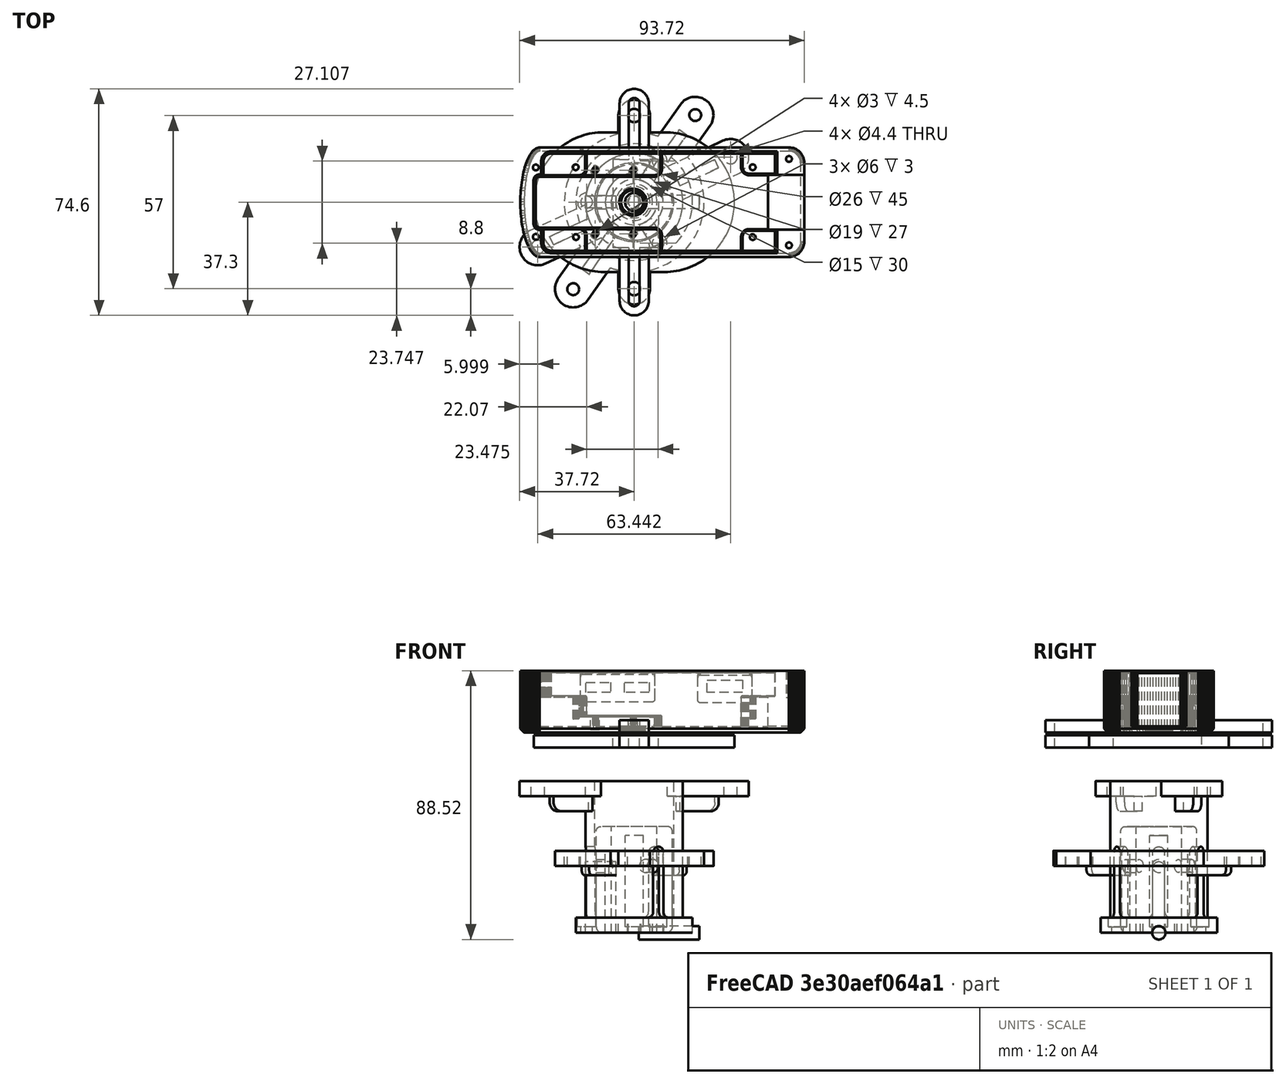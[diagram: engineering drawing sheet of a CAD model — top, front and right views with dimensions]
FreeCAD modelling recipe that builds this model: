
FCSTD DOCUMENT  (FreeCAD 0.19R)
Label: microscope_camera_adapter_less_bolts
License: All rights reserved
LicenseURL: http://en.wikipedia.org/wiki/All_rights_reserved
objects: Part::Cylinder×18, Part::MultiFuse×12, Part::FeaturePython×9, Part::Cut×7, Part::Box×6, Part::Fillet×5, App::Part×3, Part::Feature×2, Spreadsheet::Sheet×1
note: 50 computed .brp shape members not serialized (recipe doc carries the construction recipe); baked Part::Feature solids carry a one-line shape summary decoded from their .brp

FEATURE [Spreadsheet::Sheet] Spreadsheet  label="p"
  cells = A1=plug_h; B1(plug_h)==30mm; A2=plug_central_hole_r; B2(plug_central_hole_r)==15mm; A3=plug_wall; B3(plug_wall)==5mm; A4=plug_wall_gap; B4(plug_wall_gap)==0.5mm; A5=top_block_h; B5(top_block_h)==47mm; A6=top_block_wall; B6(top_block_wall)==3mm; A7=top_block_bottom_wall; B7(top_block_bottom_wall)==2mm; A8=bolt_hole_r; B8(bolt_hole_r)==1.95mm; A9=insert_hole_r; B9(insert_hole_r)==2.2mm; A10=bolt_hole_size; B10(bolt_hole_size)==15mm; A11=plug_hole_z; B11(plug_hole_z)==5mm; A12=top_block_hole_offset_z; B12(top_block_hole_offset_z)==10mm; A13=camera_attachment_wall; B13(camera_attachment_wall)==5mm; A14=camera_attachment_h; B14(camera_attachment_h)==4mm; A15=top_attachment_disk_r; B15(top_attachment_disk_r)==19.2mm; A16=top_attachment_disk_h; B16(top_attachment_disk_h)==5mm; A17=top_attachment_hole_r; B17(top_attachment_hole_r)==11.5mm; A18=bolt_head_h; B18(bolt_head_h)==3mm; A19=bolt_head_r; B19(bolt_head_r)==3mm; A20=top_attachment_expanding_h; B20(top_attachment_expanding_h)==10mm; A21=top_attachment_expanding_r; B21(top_attachment_expanding_r)==top_attachment_disk_r + top_block_wall + 1mm; A22=top_lower_part_h; B22(top_lower_part_h)==30mm; A23=inserter_wall; B23(inserter_wall)==5mm; A24=inserter_hole_pos; B24(inserter_hole_pos)==13mm; A25=middle_part_h; B25(middle_part_h)==45mm; A26=middle_bolt_hole_size; B26(middle_bolt_hole_size)==top_lower_part_h - inserter_hole_pos + insert_hole_r * 2; A27=spring_r; B27(spring_r)==5mm; A28=spring_border; B28(spring_border)==1mm; A29=sprint_dist; B29(sprint_dist)==70mm; A30=outer_cylinder_r; B30(outer_cylinder_r)==top_attachment_hole_r + 1mm; A31=zero_holder_h; B31(zero_holder_h)==27mm
FEATURE [Part::Feature] Compound001  label="RPI compound001"
  Placement = pos=(0,0,61) rot=(0,0,1;3.14159rad)
  shape: bbox 109.5 x 74.6 x 20.32 mm, 7782 faces (baked)
FEATURE [Part::Cylinder] Cylinder016  label="outer cylinder"
  Angle = 360
  AttacherType = Attacher::AttachEngine3D
  Height = 35
  Radius = 12.5
  expr: Radius = <<p>>.outer_cylinder_r
  expr: Height = <<p>>.top_lower_part_h + <<p>>.top_attachment_disk_h
FEATURE [Part::Cylinder] Cylinder018  label="top attachment bolt hole001"
  Angle = 360
  AttacherType = Attacher::AttachEngine3D
  Height = 30
  Radius = 1.95
  expr: Radius = <<p>>.bolt_hole_r
FEATURE [Part::Cylinder] Cylinder019  label="top attachment disk001"
  Angle = 360
  AttacherType = Attacher::AttachEngine3D
  Height = 5
  Radius = 19.2
  expr: Radius = <<p>>.top_attachment_disk_r
  expr: Height = <<p>>.top_attachment_disk_h
FEATURE [Part::Cylinder] Cylinder020  label="inner cylinder"
  Angle = 360
  AttacherType = Attacher::AttachEngine3D
  Height = 52
  Radius = 7.5
  expr: Height = <<p>>.top_block_h + <<p>>.top_attachment_disk_h
  expr: Radius = <<p>>.outer_cylinder_r - <<p>>.inserter_wall
FEATURE [Part::Cylinder] Cylinder021  label="top attachment bolt head hole001"
  Angle = 360
  AttacherType = Attacher::AttachEngine3D
  Height = 30
  Placement = pos=(0,0,2) rot=(0,0,1;0rad)
  Radius = 3
  expr: Radius = <<p>>.bolt_head_r
  expr: .Placement.Base.z = <<p>>.top_attachment_disk_h - <<p>>.bolt_head_h
FEATURE [Part::MultiFuse] Fusion011  label="bolt hole fusion002"
  Shapes = -> [Cylinder018,Cylinder021]
FEATURE [Part::FeaturePython] Array007  label="top attachment bolt hole array001"  # Draft array (typed FeaturePython)
  Angle = 360
  ArrayType = 2
  Axis = (0,0,1)
  Base = -> Fusion011
  Center = (0,0,0)
  Count = 4
  ExpandArray = false
  Fuse = false
  IntervalAxis = (0,0,0)
  IntervalX = (50,0,0)
  IntervalY = (0,50,0)
  IntervalZ = (0,0,50)
  NumberCircles = 2
  NumberPolar = 5
  NumberX = 2
  NumberY = 2
  NumberZ = 1
  PlacementList = 4 placements: [(0,0,0),(-15.65,0,0),(7.825,-13.5533,0),(7.825,13.5533,0)]
  RadialDistance = 15.65
  ScaleList = (4) [(1,1,1),(1,1,1),(1,1,1),(1,1,1)]
  Symmetry = 1
  TangentialDistance = 30
  expr: RadialDistance = <<p>>.top_attachment_hole_r + (<<p>>.top_attachment_disk_r - <<p>>.top_attachment_hole_r) / 2 + 0.3mm
FEATURE [Part::Cylinder] Cylinder023  label="insert hole001"
  Angle = 360
  AttacherType = Attacher::AttachEngine3D
  Height = 20
  Placement = pos=(21.5,0,0) rot=(0,-1,0;1.5708rad)
  Radius = 2.2
  expr: .Placement.Base.x = <<p>>.top_attachment_hole_r + Height / 2
  expr: Radius = <<p>>.insert_hole_r
FEATURE [Part::FeaturePython] Array009  label="insert hole polar array001"  # Draft array (typed FeaturePython)
  Angle = 360
  ArrayType = 1
  Axis = (0,0,1)
  Base = -> Cylinder023
  Center = (0,0,0)
  Count = 3
  ExpandArray = false
  Fuse = false
  IntervalAxis = (0,0,0)
  IntervalX = (50,0,0)
  IntervalY = (0,50,0)
  IntervalZ = (0,0,50)
  NumberCircles = 3
  NumberPolar = 3
  NumberX = 2
  NumberY = 2
  NumberZ = 1
  Placement = pos=(0,0,22) rot=(0,0,1;1.0472rad)
  PlacementList = 3 placements: [(21.5,0,0),(-10.75,18.6195,0),(-10.75,-18.6195,0)]
  RadialDistance = 50
  ScaleList = (3) [(1,1,1),(1,1,1),(1,1,1)]
  Symmetry = 1
  TangentialDistance = 25
  expr: .Placement.Base.z = <<p>>.top_attachment_disk_h + <<p>>.top_lower_part_h - <<p>>.inserter_hole_pos
FEATURE [Part::MultiFuse] Fusion010  label="top attachment hole fusion001"
  Shapes = -> [Array009,Cylinder020]
FEATURE [Part::Cut] Cut007  label="top lower pipe"
  Base = -> Cylinder016
  Tool = -> Cylinder020
FEATURE [Part::Fillet] Fillet002  label="top lower pipe fillet"
  Base = -> Cut007
  Edges = 1 edges r=1.5: [Edge1]
FEATURE [Part::MultiFuse] Fusion012  label="body fusion001"
  Shapes = -> [Cylinder019,Fillet002]
FEATURE [Part::Cylinder] Cylinder024  label="internal cylinder"
  Angle = 360
  AttacherType = Attacher::AttachEngine3D
  Height = 45
  Placement = pos=(0,0,5) rot=(0,0,1;0rad)
  Radius = 13
  expr: .Placement.Base.z = <<p>>.top_attachment_disk_h
  expr: Height = <<p>>.middle_part_h
  expr: Radius = <<p>>.outer_cylinder_r + <<p>>.plug_wall_gap
FEATURE [Part::Cylinder] Cylinder025  label="external cylinder001"
  Angle = 360
  AttacherType = Attacher::AttachEngine3D
  Height = 45
  Placement = pos=(0,0,5) rot=(0,0,1;0rad)
  Radius = 16
  expr: .Placement.Base.z = <<p>>.top_attachment_disk_h
  expr: Height = <<p>>.middle_part_h
  expr: Radius = <<internal cylinder>>.Radius + <<p>>.top_block_wall
FEATURE [Part::Cylinder] Cylinder026  label="hole side001"
  Angle = 360
  AttacherType = Attacher::AttachEngine3D
  Height = 10
  Placement = pos=(21.4,0,0) rot=(0,0,1;0rad)
  Radius = 1.95
  expr: .Placement.Base.x = <<p>>.middle_bolt_hole_size
  expr: Radius = <<p>>.bolt_hole_r
FEATURE [Part::Box] Box002  label="camera hole central cube001"
  AttacherType = Attacher::AttachEngine3D
  Height = 10
  Length = 21.4
  Placement = pos=(0,-1.95,0) rot=(0,0,1;0rad)
  Width = 3.9
  expr: .Placement.Base.y = -<<p>>.bolt_hole_r
  expr: Width = <<p>>.bolt_hole_r * 2
  expr: Length = <<p>>.middle_bolt_hole_size
FEATURE [Part::MultiFuse] Fusion013  label="bolt hole fusion003"
  Placement = pos=(-6,0,0) rot=(0,-1,0;1.5708rad)
  Shapes = -> [Box002,Cylinder026]
  expr: .Placement.Base.x = -<<external cylinder001>>.Radius + <<hole side001>>.Height
FEATURE [Part::FeaturePython] Array011  label="bolt hole polar array001"  # Draft array (typed FeaturePython)
  Angle = 360
  ArrayType = 1
  Axis = (0,0,1)
  Base = -> Fusion013
  Center = (0,0,0)
  Count = 3
  ExpandArray = false
  Fuse = false
  IntervalAxis = (0,0,0)
  IntervalX = (50,0,0)
  IntervalY = (0,50,0)
  IntervalZ = (0,0,50)
  NumberCircles = 3
  NumberPolar = 3
  NumberX = 2
  NumberY = 2
  NumberZ = 1
  Placement = pos=(0,0,5) rot=(0,0,1;0rad)
  PlacementList = 3 placements: [(-6,0,0),(3,-5.19615,0),(3,5.19615,0)]
  RadialDistance = 50
  ScaleList = (3) [(1,1,1),(1,1,1),(1,1,1)]
  Symmetry = 1
  TangentialDistance = 25
  expr: .Placement.Base.z = <<external cylinder001>>.Placement.Base.z
FEATURE [Part::MultiFuse] Fusion014  label="middle hole fusion"
  Shapes = -> [Array011,Cylinder024]
FEATURE [Part::Cylinder] Cylinder027  label="spring plate end"
  Angle = 360
  AttacherType = Attacher::AttachEngine3D
  Height = 5
  Radius = 6
  expr: Height = <<p>>.inserter_wall
  expr: Radius = <<p>>.spring_r + <<p>>.spring_border
FEATURE [Part::FeaturePython] Array012  label="spring plate end array"  # Draft array (typed FeaturePython)
  Angle = 360
  ArrayType = 0
  Axis = (0,0,1)
  Base = -> Cylinder027
  Center = (0,0,0)
  Count = 2
  ExpandArray = false
  Fuse = false
  IntervalAxis = (0,0,0)
  IntervalX = (70,0,0)
  IntervalY = (0,100,0)
  IntervalZ = (0,0,100)
  NumberCircles = 3
  NumberPolar = 5
  NumberX = 2
  NumberY = 1
  NumberZ = 1
  PlacementList = 2 placements: [(0,0,0),(70,0,0)]
  RadialDistance = 50
  ScaleList = (2) [(1,1,1),(1,1,1)]
  Symmetry = 1
  TangentialDistance = 25
  expr: .IntervalX.x = <<p>>.sprint_dist
FEATURE [Part::Cylinder] Cylinder028  label="spring plate end001"
  Angle = 360
  AttacherType = Attacher::AttachEngine3D
  Height = 5
  Radius = 2.2
  expr: Radius = <<p>>.insert_hole_r
  expr: Height = <<p>>.inserter_wall
FEATURE [Part::FeaturePython] Array013  label="spring plate end array001"  # Draft array (typed FeaturePython)
  Angle = 360
  ArrayType = 0
  Axis = (0,0,1)
  Base = -> Cylinder028
  Center = (0,0,0)
  Count = 2
  ExpandArray = false
  Fuse = false
  IntervalAxis = (0,0,0)
  IntervalX = (70,0,0)
  IntervalY = (0,100,0)
  IntervalZ = (0,0,100)
  NumberCircles = 3
  NumberPolar = 5
  NumberX = 2
  NumberY = 1
  NumberZ = 1
  PlacementList = 2 placements: [(0,0,0),(70,0,0)]
  RadialDistance = 50
  ScaleList = (2) [(1,1,1),(1,1,1)]
  Symmetry = 1
  TangentialDistance = 25
  expr: .IntervalX.x = <<p>>.sprint_dist
FEATURE [Part::Box] Box003  label="spring plate cube"
  AttacherType = Attacher::AttachEngine3D
  Height = 5
  Length = 70
  Placement = pos=(0,-6,0) rot=(0,0,1;0rad)
  Width = 12
  expr: .Placement.Base.y = -Width / 2
  expr: Height = <<spring plate end>>.Height
  expr: Width = <<spring plate end>>.Radius * 2
  expr: Length = <<p>>.sprint_dist
FEATURE [Part::Cylinder] Cylinder029  label="spring plate end002"
  Angle = 360
  AttacherType = Attacher::AttachEngine3D
  Height = 5
  Radius = 6
  expr: Radius = <<p>>.spring_r + <<p>>.spring_border
  expr: Height = <<p>>.inserter_wall
FEATURE [Part::FeaturePython] Array014  label="spring plate end array002"  # Draft array (typed FeaturePython)
  Angle = 360
  ArrayType = 0
  Axis = (0,0,1)
  Base = -> Cylinder029
  Center = (0,0,0)
  Count = 2
  ExpandArray = false
  Fuse = false
  IntervalAxis = (0,0,0)
  IntervalX = (70,0,0)
  IntervalY = (0,100,0)
  IntervalZ = (0,0,100)
  NumberCircles = 3
  NumberPolar = 5
  NumberX = 2
  NumberY = 1
  NumberZ = 1
  PlacementList = 2 placements: [(0,0,0),(70,0,0)]
  RadialDistance = 50
  ScaleList = (2) [(1,1,1),(1,1,1)]
  Symmetry = 1
  TangentialDistance = 25
  expr: .IntervalX.x = <<p>>.sprint_dist
FEATURE [Part::Cylinder] Cylinder030  label="spring plate end003"
  Angle = 360
  AttacherType = Attacher::AttachEngine3D
  Height = 5
  Radius = 1.95
  expr: Height = <<p>>.inserter_wall
  expr: Radius = <<p>>.bolt_hole_r
FEATURE [Part::FeaturePython] Array015  label="spring plate end array003"  # Draft array (typed FeaturePython)
  Angle = 360
  ArrayType = 0
  Axis = (0,0,1)
  Base = -> Cylinder030
  Center = (0,0,0)
  Count = 2
  ExpandArray = false
  Fuse = false
  IntervalAxis = (0,0,0)
  IntervalX = (70,0,0)
  IntervalY = (0,100,0)
  IntervalZ = (0,0,100)
  NumberCircles = 3
  NumberPolar = 5
  NumberX = 2
  NumberY = 1
  NumberZ = 1
  PlacementList = 2 placements: [(0,0,0),(70,0,0)]
  RadialDistance = 50
  ScaleList = (2) [(1,1,1),(1,1,1)]
  Symmetry = 1
  TangentialDistance = 25
  expr: .IntervalX.x = <<p>>.sprint_dist
FEATURE [Part::Box] Box004  label="Cube"
  AttacherType = Attacher::AttachEngine3D
  Height = 5
  Length = 70
  Placement = pos=(0,-6,0) rot=(0,0,1;0rad)
  Width = 12
  expr: Length = <<p>>.sprint_dist
  expr: Width = <<spring plate end002>>.Radius * 2
  expr: Height = <<p>>.inserter_wall
  expr: .Placement.Base.y = -Width / 2
FEATURE [Part::MultiFuse] Fusion017  label="spring plate fusion001"
  Shapes = -> [Array014,Box004]
FEATURE [Part::Cut] Cut010  label="spring attachment plate001"
  Base = -> Fusion017
  Placement = pos=(-35,0,22) rot=(0,0,1;0rad)
  Tool = -> Array015
  expr: .Placement.Base.z = <<zero holder external cylinder>>.Height - <<spring plate end002>>.Height
  expr: .Placement.Base.x = -<<p>>.sprint_dist / 2
FEATURE [Part::Cylinder] Cylinder031  label="zero holder external cylinder"
  Angle = 360
  AttacherType = Attacher::AttachEngine3D
  Height = 27
  Radius = 12.5
  expr: Height = <<p>>.zero_holder_h
  expr: Radius = <<internal cylinder>>.Radius - <<p>>.plug_wall_gap
FEATURE [Part::Cylinder] Cylinder032  label="zero holder internal cylinder"
  Angle = 360
  AttacherType = Attacher::AttachEngine3D
  Height = 27
  Radius = 9.5
  expr: Radius = <<zero holder external cylinder>>.Radius - <<p>>.top_block_wall
  expr: Height = <<p>>.zero_holder_h
FEATURE [Part::Cylinder] Cylinder035  label="zero holder top disk"
  Angle = 360
  AttacherType = Attacher::AttachEngine3D
  Height = 5
  Placement = pos=(0,0,22) rot=(0,0,1;0rad)
  Radius = 23
  expr: .Placement.Base.z = <<zero holder external cylinder>>.Height - Height
  expr: Height = <<spring plate end002>>.Height
FEATURE [Part::Feature] Cut002004001  label="Pi_Zero_Case001"
  Placement = pos=(0,0,66) rot=(0,0,1;3.14159rad)
  shape: bbox 93.47 x 74.6 x 20.32 mm, 7631 faces, 7 solids (baked)
FEATURE [Part::Box] Box007  label="spring plate cube001"
  AttacherType = Attacher::AttachEngine3D
  Height = 5
  Length = 60
  Placement = pos=(5,-1.5,-5) rot=(0,0,1;0rad)
  Width = 3
  expr: .Placement.Base.z = -<<spring plate end>>.Height
  expr: Length = <<p>>.sprint_dist - 10mm
  expr: Height = <<spring plate end>>.Height
  expr: .Placement.Base.y = -Width / 2
FEATURE [Part::Fillet] Fillet003
  Base = -> Box007
  Edges = 2 edges r=3: [Edge4,Edge8]
FEATURE [Part::MultiFuse] Fusion015  label="spring plate fusion"
  Shapes = -> [Array012,Box003,Fillet003]
FEATURE [Part::Cut] Cut009  label="spring attachment plate"
  Base = -> Fusion015
  Placement = pos=(-35,0,45) rot=(0,0,1;0rad)
  Tool = -> Array013
  expr: .Placement.Base.x = -<<p>>.sprint_dist / 2
  expr: .Placement.Base.z = <<p>>.middle_part_h
FEATURE [Part::MultiFuse] Fusion016  label="middle body fusion"
  Placement = pos=(0,0,0) rot=(0,0,1;0.436332rad)
  Shapes = -> [Cylinder025,Cut009]
FEATURE [Part::Cut] Cut008  label="middle cut"
  Base = -> Fusion016
  Tool = -> Fusion014
FEATURE [Part::Cylinder] Cylinder046  label="insert hole"
  Angle = 360
  AttacherType = Attacher::AttachEngine3D
  Height = 5
  Radius = 2.2
  expr: Height = <<p>>.inserter_wall
  expr: Radius = <<p>>.insert_hole_r
FEATURE [Part::Cylinder] Cylinder048  label="bolt wall"
  Angle = 360
  AttacherType = Attacher::AttachEngine3D
  Height = 5
  Radius = 5.2
  expr: Height = <<p>>.inserter_wall
  expr: Radius = <<insert hole>>.Radius + 3mm
FEATURE [Part::FeaturePython] Array021  label="bolt wall array"  # Draft array (typed FeaturePython)
  Angle = 360
  ArrayType = 0
  Axis = (0,0,1)
  Base = -> Cylinder048
  Center = (0,0,0)
  Count = 2
  ExpandArray = false
  Fuse = false
  IntervalAxis = (0,0,0)
  IntervalX = (100,0,0)
  IntervalY = (0,57,0)
  IntervalZ = (0,0,100)
  NumberCircles = 3
  NumberPolar = 5
  NumberX = 1
  NumberY = 2
  NumberZ = 1
  Placement = pos=(0,-28.5,0) rot=(0,0,1;0rad)
  PlacementList = 2 placements: [(0,0,0),(0,57,0)]
  RadialDistance = 50
  ScaleList = (2) [(1,1,1),(1,1,1)]
  Symmetry = 1
  TangentialDistance = 25
  expr: .IntervalY.y = <<bolt hole array>>.IntervalY.y
  expr: .Placement.Base.y = -.IntervalY.y / 2
FEATURE [Part::FeaturePython] Array022  label="bolt hole array"  # Draft array (typed FeaturePython)
  Angle = 360
  ArrayType = 0
  Axis = (0,0,1)
  Base = -> Cylinder046
  Center = (0,0,0)
  Count = 2
  ExpandArray = false
  Fuse = false
  IntervalAxis = (0,0,0)
  IntervalX = (100,0,0)
  IntervalY = (0,57,0)
  IntervalZ = (0,0,100)
  NumberCircles = 3
  NumberPolar = 5
  NumberX = 1
  NumberY = 2
  NumberZ = 1
  Placement = pos=(0,-28.5,0) rot=(0,0,1;0rad)
  PlacementList = 2 placements: [(0,0,0),(0,57,0)]
  RadialDistance = 50
  ScaleList = (2) [(1,1,1),(1,1,1)]
  Symmetry = 1
  TangentialDistance = 25
  expr: .Placement.Base.y = -.IntervalY.y / 2
FEATURE [Part::MultiFuse] Fusion025  label="extract fusion"
  Shapes = -> [Array022]
FEATURE [Part::Box] Box  label="between hole cube"
  AttacherType = Attacher::AttachEngine3D
  Height = 5
  Length = 10.4
  Placement = pos=(-5.2,-28.5,0) rot=(0,0,1;0rad)
  Width = 57
  expr: .Placement.Base.y = -Width / 2
  expr: .Placement.Base.x = -Length / 2
  expr: Length = <<bolt wall>>.Radius * 2
  expr: Height = <<p>>.inserter_wall
  expr: Width = <<bolt hole array>>.IntervalY.y
FEATURE [Part::MultiFuse] Fusion023  label="bolt wall fusion"
  Shapes = -> [Array021,Box]
FEATURE [Part::Cut] Cut002004004  label="microscope attachment cut"
  Base = -> Fusion023
  Placement = pos=(0,0,22) rot=(0,0,1;-0.959931rad)
  Tool = -> Fusion025
  expr: .Placement.Base.z = <<p>>.zero_holder_h - <<p>>.inserter_wall
FEATURE [Part::Box] Box008  label="spring plate cube002"
  AttacherType = Attacher::AttachEngine3D
  Height = 3
  Length = 56
  Placement = pos=(-28,-1.5,19) rot=(0,0,1;0rad)
  Width = 3
  expr: .Placement.Base.x = -Length / 2
  expr: .Placement.Base.y = -Width / 2
  expr: Length = <<p>>.sprint_dist - 14mm
  expr: .Placement.Base.z = <<p>>.zero_holder_h - Height - <<p>>.inserter_wall
FEATURE [Part::Fillet] Fillet004  label="sprint plate fillet"
  Base = -> Box008
  Edges = 2 edges r=1.6: [Edge4,Edge8]
FEATURE [Part::Fillet] Fillet  label="zero holder external cylinder fillet"
  Base = -> Cylinder031
  Edges = 1 edges r=2: [Edge3]
FEATURE [Part::MultiFuse] Fusion018  label="zero holder fusion"
  Placement = pos=(0,0,0) rot=(0,0,1;0.959931rad)
  Shapes = -> [Cut010,Cylinder035,Cut002004004,Fillet004,Fillet]
FEATURE [Part::Cut] Cut011  label="zero holder cut"
  Base = -> Fusion018
  Tool = -> Cylinder032
FEATURE [App::Part] Part006  label="zero holder part"
  Group = -> [Cut011]
  Origin = -> Origin009
  Placement = pos=(0,0,41) rot=(0,0,1;0rad)
FEATURE [Part::Fillet] Fillet005  label="middle cut fillet"
  Base = -> Cut008
  Edges = 6 edges r=2: [Edge67,Edge68,Edge72,Edge73,Edge77,Edge78]
FEATURE [App::Part] Part005  label="top middle part"
  Group = -> [Cut008,Fillet005]
  Origin = -> Origin008
  Placement = pos=(0,0,0) rot=(0,0,1;0.523599rad)
FEATURE [Part::MultiFuse] Fusion  label="top attachment extract fusion"
  Shapes = -> [Fusion010,Array007]
FEATURE [Part::Cut] Cut005  label="top attachment disk cut001"
  Base = -> Fusion012
  Tool = -> Fusion
FEATURE [App::Part] Part003  label="top bolted narrow lower part"
  Group = -> [Cut005]
  Origin = -> Origin004
  Placement = pos=(0,0,0) rot=(0,0,1;0.523599rad)
